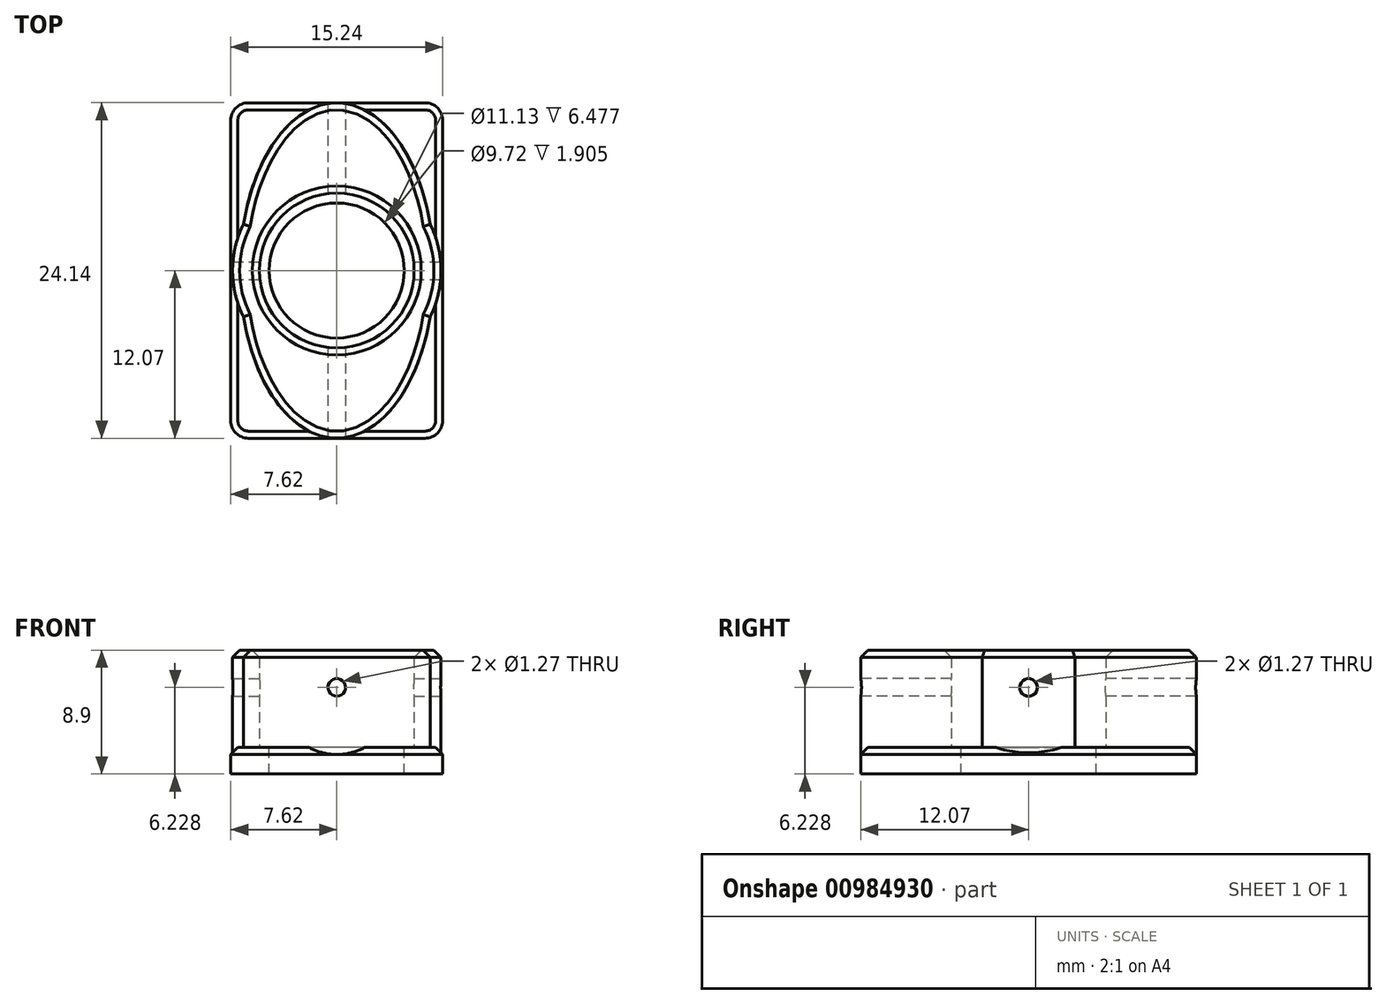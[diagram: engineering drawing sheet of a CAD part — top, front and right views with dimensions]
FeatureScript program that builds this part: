
annotation { "Feature Type Name" : "Feature", "Feature Type Description" : "" }
export const myFeature = defineFeature(function(context is Context, id is Id, definition is map)
    precondition{}
    {
        {
            var Q0;
            Q0=qCreatedBy(makeId("Top.planeOp"),FACE);
            var sketch = newSketch(context, id + "F0", { "sketchPlane" : qUnion([Q0])});
            skPoint(sketch, "E0.middle", {"position": v(0, 0) * mm});
            skCircle(sketch, "E1", {"center": v(0, 0) * mm, "radius": 7.5 * mm});
            skCircle(sketch, "E2", {"center": v(0, 0) * mm, "radius": 5.56 * mm});
            skEllipse(sketch, "E3", {"center": v(0, 0) * mm, "majorRadius": 12.07 * mm, "minorRadius": 6.99 * mm, "majorAxis": v(0, 1)});
            skSolve(sketch);
        }
        {
            var Q0;
            Q0=makeQuery(id+"F0.imprint","IMPRINT",FACE,{"disambiguationData":[TD([[makeQuery(id+"F0.imprint","IMPRINT",EDGE,{"derivedFrom":sQuery(id+"F0.wireOp",EDGE,"E1")}),1.0]])]});
            var Q1;
            {var subQ0=sQuery(id+"F0.wireOp",EDGE,"E3");var subQ1=sQuery(id+"F0.wireOp",EDGE,"E1");var subQ2=makeQuery(id+"F0.imprint","INTERSECT",VERTEX,{"disambiguationData":[OD(0.0)],"derivedFrom":[subQ1,subQ0]});Q1=makeQuery(id+"F0.imprint","IMPRINT",FACE,{"disambiguationData":[TD([[makeQuery(id+"F0.imprint","IMPRINT",EDGE,{"disambiguationData":[TD([[subQ2,1.0]])],"derivedFrom":subQ1}),-1.0]])]});}
            var Q2;
            {var subQ0=sQuery(id+"F0.wireOp",EDGE,"E3");var subQ1=sQuery(id+"F0.wireOp",EDGE,"E1");var subQ2=makeQuery(id+"F0.imprint","INTERSECT",VERTEX,{"disambiguationData":[OD(2.0)],"derivedFrom":[subQ1,subQ0]});Q2=makeQuery(id+"F0.imprint","IMPRINT",FACE,{"disambiguationData":[TD([[makeQuery(id+"F0.imprint","IMPRINT",EDGE,{"disambiguationData":[TD([[subQ2,-1.0]])],"derivedFrom":subQ1}),-1.0]])]});}
            var Q3;
            {var subQ0=sQuery(id+"F0.wireOp",EDGE,"E3");var subQ1=sQuery(id+"F0.wireOp",EDGE,"E1");var subQ2=makeQuery(id+"F0.imprint","INTERSECT",VERTEX,{"disambiguationData":[OD(0.0)],"derivedFrom":[subQ1,subQ0]});Q3=makeQuery(id+"F0.imprint","IMPRINT",FACE,{"disambiguationData":[TD([[makeQuery(id+"F0.imprint","IMPRINT",EDGE,{"disambiguationData":[TD([[subQ2,-1.0]])],"derivedFrom":subQ1}),1.0]])]});}
            var Q4;
            {var subQ0=sQuery(id+"F0.wireOp",EDGE,"E3");var subQ1=sQuery(id+"F0.wireOp",EDGE,"E1");var subQ2=makeQuery(id+"F0.imprint","INTERSECT",VERTEX,{"disambiguationData":[OD(1.0)],"derivedFrom":[subQ1,subQ0]});Q4=makeQuery(id+"F0.imprint","IMPRINT",FACE,{"disambiguationData":[TD([[makeQuery(id+"F0.imprint","IMPRINT",EDGE,{"disambiguationData":[TD([[subQ2,1.0]])],"derivedFrom":subQ1}),1.0]])]});}
            extrude(context, id + "F1", {"entities" : qUnion([Q0, Q1, Q2, Q3, Q4]), "depth" : 7 * mm, "offsetDistance" : 25.4 * mm});
        }
        {
            var Q0;
            Q0=qCreatedBy(makeId("Right.planeOp"),FACE);
            var sketch = newSketch(context, id + "F2", { "sketchPlane" : qUnion([Q0])});
            skCircle(sketch, "E4", {"center": v(0, 4.32) * mm, "radius": 0.64 * mm});
            skSolve(sketch);
        }
        {
            var Q0;
            Q0=makeQuery(id+"F2.imprint","IMPRINT",FACE,{"disambiguationData":[TD([[makeQuery(id+"F2.imprint","IMPRINT",EDGE,{"derivedFrom":sQuery(id+"F2.wireOp",EDGE,"E4")}),1.0]])]});
            extrude(context, id + "F3", {"entities" : qUnion([Q0]), "operationType" : NewBodyOperationType.REMOVE, "endBound" : BoundingType.SYMMETRIC, "oppositeDirection" : true, "depth" : 50.8 * mm, "offsetDistance" : 25.4 * mm});
        }
        {
            var Q0;
            Q0=qCreatedBy(makeId("Front.planeOp"),FACE);
            var sketch = newSketch(context, id + "F4", { "sketchPlane" : qUnion([Q0])});
            skCircle(sketch, "E5", {"center": v(0, 4.32) * mm, "radius": 0.64 * mm});
            skSolve(sketch);
        }
        {
            var Q0;
            Q0=qCreatedBy(makeId("Top.planeOp"),FACE);
            var sketch = newSketch(context, id + "F5", { "sketchPlane" : qUnion([Q0])});
            skLineSegment(sketch, "E6.bottom", {"start": v(7.62, 12.07) * mm, "end": v(-7.62, 12.07) * mm});
            skLineSegment(sketch, "E6.top", {"start": v(7.62, -12.07) * mm, "end": v(-7.62, -12.07) * mm});
            skLineSegment(sketch, "E6.left", {"start": v(7.62, 12.07) * mm, "end": v(7.62, -12.07) * mm});
            skLineSegment(sketch, "E6.right", {"start": v(-7.62, 12.07) * mm, "end": v(-7.62, -12.07) * mm});
            skPoint(sketch, "E6.middle", {"position": v(0, 0) * mm});
            skSolve(sketch);
        }
        {
            var Q0;
            Q0=makeQuery(id+"F5.imprint","IMPRINT",FACE,{"disambiguationData":[TD([[makeQuery(id+"F5.imprint","IMPRINT",EDGE,{"derivedFrom":sQuery(id+"F5.wireOp",EDGE,"E6.bottom")}),1.0]])]});
            extrude(context, id + "F6", {"entities" : qUnion([Q0]), "operationType" : NewBodyOperationType.ADD, "oppositeDirection" : true, "depth" : 1.9 * mm, "offsetDistance" : 25.4 * mm});
        }
        {
            var Q0;
            {var subQ0=sQuery(id+"F5.wireOp",EDGE,"E6.left");var subQ1=sQuery(id+"F5.wireOp",EDGE,"E6.bottom");var subQ2=sQuery(id+"F5.wireOp",EDGE,"E6.top");var subQ3=sQuery(id+"F5.wireOp",EDGE,"E6.right");Q0=makeQuery(id+"F6.boolean.opBoolean","SPLIT",FACE,{"disambiguationData":[TD([makeQuery(id+"F1.opExtrude","SWEPT_FACE",FACE,{"disambiguationData":[OSD([sQuery(id+"F0.wireOp",EDGE,"E1")])]})])],"derivedFrom":makeQuery(id+"F6.opExtrude","CAP_FACE",FACE,{"disambiguationData":[OSD([subQ1,subQ2,subQ0,subQ3])],"isStart":true})});}
            var sketch = newSketch(context, id + "F7", { "sketchPlane" : qUnion([Q0])});
            skCircle(sketch, "E7", {"center": v(0, 0) * mm, "radius": 4.86 * mm});
            skSolve(sketch);
        }
        {
            var Q0;
            Q0=makeQuery(id+"F7.imprint","IMPRINT",FACE,{"disambiguationData":[TD([[makeQuery(id+"F7.imprint","IMPRINT",EDGE,{"derivedFrom":sQuery(id+"F7.wireOp",EDGE,"E7")}),1.0]])]});
            extrude(context, id + "F8", {"entities" : qUnion([Q0]), "operationType" : NewBodyOperationType.REMOVE, "oppositeDirection" : true, "depth" : 2.54 * mm, "offsetDistance" : 25.4 * mm});
        }
        {
            var Q0;
            Q0=makeQuery(id+"F6.opExtrude","SWEPT_EDGE",EDGE,{"disambiguationData":[OSD([sQuery(id+"F5.wireOp",EDGE,"E6.bottom"),sQuery(id+"F5.wireOp",EDGE,"E6.left")])]});
            var Q1;
            Q1=makeQuery(id+"F6.opExtrude","SWEPT_EDGE",EDGE,{"disambiguationData":[OSD([sQuery(id+"F5.wireOp",EDGE,"E6.bottom"),sQuery(id+"F5.wireOp",EDGE,"E6.right")])]});
            var Q2;
            Q2=makeQuery(id+"F6.opExtrude","SWEPT_EDGE",EDGE,{"disambiguationData":[OSD([sQuery(id+"F5.wireOp",EDGE,"E6.top"),sQuery(id+"F5.wireOp",EDGE,"E6.right")])]});
            var Q3;
            Q3=makeQuery(id+"F6.opExtrude","SWEPT_EDGE",EDGE,{"disambiguationData":[OSD([sQuery(id+"F5.wireOp",EDGE,"E6.top"),sQuery(id+"F5.wireOp",EDGE,"E6.left")])]});
            fillet(context, id + "F9", {"entities" : qUnion([Q0, Q1, Q2, Q3]), "radius" : 1.27 * mm, "tangentPropagation" : true, "allowEdgeOverflow" : false});
        }
        {
            var Q0;
            {var subQ0=sQuery(id+"F0.wireOp",EDGE,"E3");var subQ1=sQuery(id+"F0.wireOp",EDGE,"E1");Q0=makeQuery(id+"F1.opExtrude","CAP_EDGE",EDGE,{"disambiguationData":[OSD([subQ0]),TDD([makeQuery(id+"F0.imprint","IMPRINT",EDGE,{"disambiguationData":[TD([[makeQuery(id+"F0.imprint","INTERSECT",VERTEX,{"disambiguationData":[OD(2.0)],"derivedFrom":[subQ1,subQ0]}),-1.0]])],"derivedFrom":subQ0})])],"isStart":false});}
            var Q1;
            {var subQ0=sQuery(id+"F0.wireOp",EDGE,"E3");var subQ1=sQuery(id+"F0.wireOp",EDGE,"E1");Q1=makeQuery(id+"F1.opExtrude","CAP_EDGE",EDGE,{"disambiguationData":[OSD([subQ0]),TDD([makeQuery(id+"F0.imprint","IMPRINT",EDGE,{"disambiguationData":[TD([[makeQuery(id+"F0.imprint","INTERSECT",VERTEX,{"disambiguationData":[OD(0.0)],"derivedFrom":[subQ1,subQ0]}),1.0]])],"derivedFrom":subQ0})])],"isStart":false});}
            var Q2;
            {var subQ0=sQuery(id+"F0.wireOp",EDGE,"E3");var subQ1=sQuery(id+"F0.wireOp",EDGE,"E1");Q2=makeQuery(id+"F1.opExtrude","CAP_EDGE",EDGE,{"disambiguationData":[OSD([subQ1]),TDD([makeQuery(id+"F0.imprint","IMPRINT",EDGE,{"disambiguationData":[TD([[makeQuery(id+"F0.imprint","INTERSECT",VERTEX,{"disambiguationData":[OD(1.0)],"derivedFrom":[subQ1,subQ0]}),1.0]])],"derivedFrom":subQ1})])],"isStart":false});}
            var Q3;
            {var subQ0=sQuery(id+"F0.wireOp",EDGE,"E3");var subQ1=sQuery(id+"F0.wireOp",EDGE,"E1");Q3=makeQuery(id+"F1.opExtrude","CAP_EDGE",EDGE,{"disambiguationData":[OSD([subQ1]),TDD([makeQuery(id+"F0.imprint","IMPRINT",EDGE,{"disambiguationData":[TD([[makeQuery(id+"F0.imprint","INTERSECT",VERTEX,{"disambiguationData":[OD(0.0)],"derivedFrom":[subQ1,subQ0]}),-1.0]])],"derivedFrom":subQ1})])],"isStart":false});}
            var Q4;
            Q4=makeQuery(id+"F1.opExtrude","CAP_EDGE",EDGE,{"disambiguationData":[OSD([sQuery(id+"F0.wireOp",EDGE,"E2")])],"isStart":false});
            var Q5;
            Q5=makeQuery(id+"F6.opExtrude","CAP_EDGE",EDGE,{"disambiguationData":[OSD([sQuery(id+"F5.wireOp",EDGE,"E6.left")])],"isStart":true});
            chamfer(context, id + "F10", {"entities" : qUnion([Q0, Q1, Q2, Q3, Q4, Q5]), "width" : 0.5 * mm, "tangentPropagation" : true});
        }
        {
            var Q0;
            Q0=makeQuery(id+"F4.imprint","IMPRINT",FACE,{"disambiguationData":[TD([[makeQuery(id+"F4.imprint","IMPRINT",EDGE,{"derivedFrom":sQuery(id+"F4.wireOp",EDGE,"E5")}),1.0]])]});
            extrude(context, id + "F11", {"entities" : qUnion([Q0]), "operationType" : NewBodyOperationType.REMOVE, "endBound" : BoundingType.SYMMETRIC, "oppositeDirection" : true, "depth" : 25.4 * mm, "offsetDistance" : 25.4 * mm});
        }
    });
